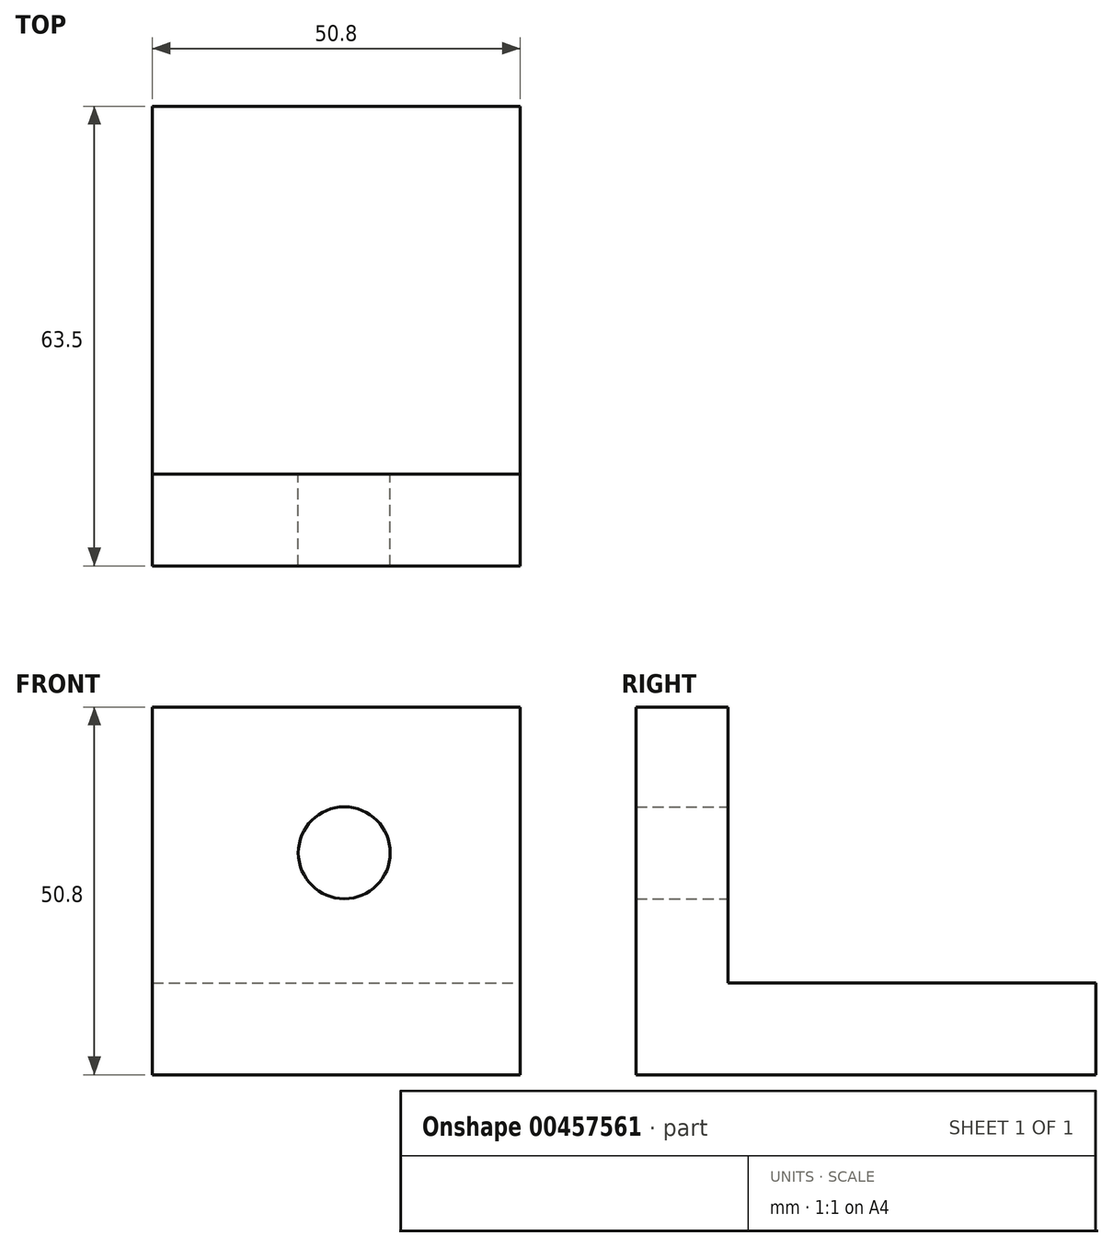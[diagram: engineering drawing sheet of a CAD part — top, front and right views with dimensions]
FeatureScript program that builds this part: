
annotation { "Feature Type Name" : "Feature", "Feature Type Description" : "" }
export const myFeature = defineFeature(function(context is Context, id is Id, definition is map)
    precondition{}
    {
        {
            var Q0;
            Q0=qCreatedBy(makeId("Top.planeOp"),FACE);
            var sketch = newSketch(context, id + "F0", { "sketchPlane" : qUnion([Q0])});
            skLineSegment(sketch, "E0.bottom", {"start": v(-26.51, 34.87) * mm, "end": v(24.29, 34.87) * mm});
            skLineSegment(sketch, "E0.top", {"start": v(-26.51, -15.93) * mm, "end": v(24.29, -15.93) * mm});
            skLineSegment(sketch, "E0.left", {"start": v(-26.51, 34.87) * mm, "end": v(-26.51, -15.93) * mm});
            skLineSegment(sketch, "E0.right", {"start": v(24.29, 34.87) * mm, "end": v(24.29, -15.93) * mm});
            skSolve(sketch);
        }
        {
            var Q0;
            Q0=makeQuery(id+"F0.imprint","IMPRINT",FACE,{"disambiguationData":[TD([[makeQuery(id+"F0.imprint","IMPRINT",EDGE,{"derivedFrom":sQuery(id+"F0.wireOp",EDGE,"E0.bottom")}),-1.0]])]});
            extrude(context, id + "F1", {"entities" : qUnion([Q0]), "depth" : 12.7 * mm});
        }
        {
            var Q0;
            Q0=makeQuery(id+"F1.opExtrude","SWEPT_FACE",FACE,{"disambiguationData":[OSD([sQuery(id+"F0.wireOp",EDGE,"E0.top")])]});
            var sketch = newSketch(context, id + "F2", { "sketchPlane" : qUnion([Q0])});
            skLineSegment(sketch, "E1.bottom", {"start": v(24.29, 0) * mm, "end": v(-26.51, 0) * mm});
            skLineSegment(sketch, "E1.top", {"start": v(24.29, 0) * mm, "end": v(-26.51, 0) * mm});
            skLineSegment(sketch, "E1.left", {"start": v(24.29, 0) * mm, "end": v(24.29, 0) * mm});
            skLineSegment(sketch, "E1.right", {"start": v(-26.51, 0) * mm, "end": v(-26.51, 0) * mm});
            skLineSegment(sketch, "E2.bottom", {"start": v(-26.51, 0) * mm, "end": v(24.29, 0) * mm});
            skLineSegment(sketch, "E2.top", {"start": v(-26.51, 50.8) * mm, "end": v(24.29, 50.8) * mm});
            skLineSegment(sketch, "E2.left", {"start": v(-26.51, 0) * mm, "end": v(-26.51, 50.8) * mm});
            skLineSegment(sketch, "E2.right", {"start": v(24.29, 0) * mm, "end": v(24.29, 50.8) * mm});
            skSolve(sketch);
        }
        {
            var Q0;
            Q0 = qSketchRegion(id + "F2", true);
            extrude(context, id + "F3", {"entities" : qUnion([Q0]), "operationType" : NewBodyOperationType.ADD, "depth" : 12.7 * mm});
        }
        {
            var Q0;
            Q0=makeQuery(id+"F3.opExtrude","CAP_FACE",FACE,{"disambiguationData":[OSD([sQuery(id+"F2.wireOp",EDGE,"E2.bottom"),sQuery(id+"F2.wireOp",EDGE,"E2.top"),sQuery(id+"F2.wireOp",EDGE,"E2.left"),sQuery(id+"F2.wireOp",EDGE,"E2.right")])],"isStart":true});
            var sketch = newSketch(context, id + "F4", { "sketchPlane" : qUnion([Q0])});
            skCircle(sketch, "E3", {"center": v(0, 30.66) * mm, "radius": 6.35 * mm});
            skSolve(sketch);
        }
        {
            var Q0;
            Q0=sQuery(id+"F4.wireOp",VERTEX,"E3.center");
            var Q1;
            Q1=makeQuery(id+"F1.opExtrude","SWEPT_BODY",BODY,{"disambiguationData":[OSD([sQuery(id+"F0.wireOp",EDGE,"E0.bottom"),sQuery(id+"F0.wireOp",EDGE,"E0.top"),sQuery(id+"F0.wireOp",EDGE,"E0.left"),sQuery(id+"F0.wireOp",EDGE,"E0.right")])]});
            hole(context, id + "F5", {"style" : HoleStyle.SIMPLE, "endStyle" : HoleEndStyle.THROUGH, "holeDiameter" : 12.7 * mm, "isTappedThrough" : true, "tappedDepth" : 12.7 * mm, "tapClearance" : 3, "locations" : qUnion([Q0]), "scope" : qUnion([Q1])});
        }
    });
